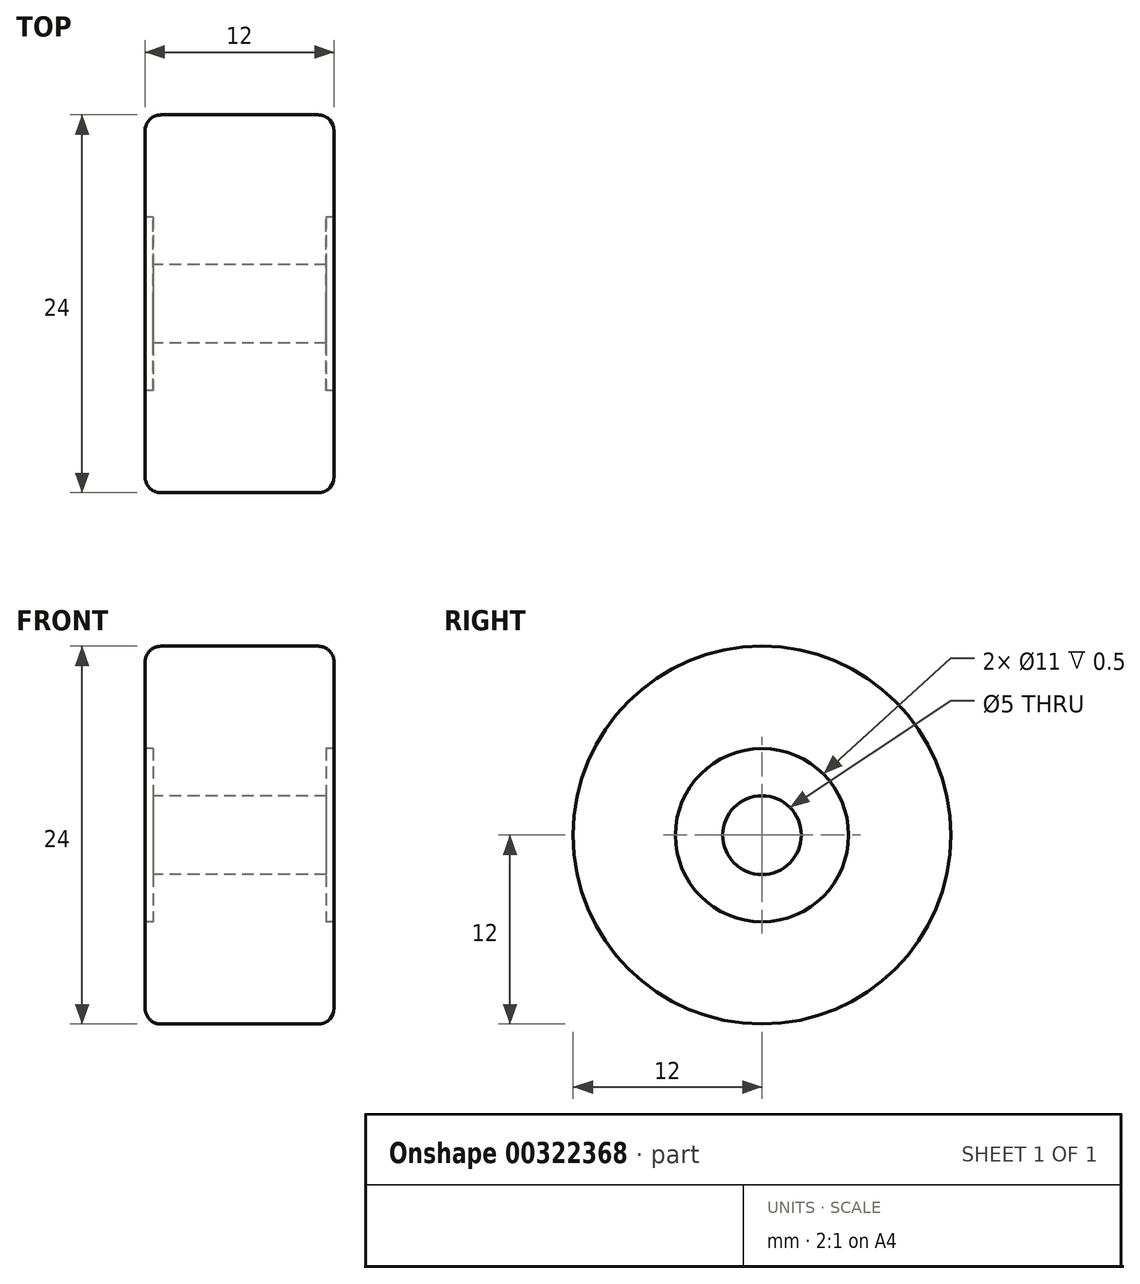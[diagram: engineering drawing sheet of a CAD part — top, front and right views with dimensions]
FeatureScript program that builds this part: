
annotation { "Feature Type Name" : "Feature", "Feature Type Description" : "" }
export const myFeature = defineFeature(function(context is Context, id is Id, definition is map)
    precondition{}
    {
        {
            var Q0;
            Q0=qCreatedBy(makeId("Top.planeOp"),FACE);
            var sketch = newSketch(context, id + "F0", { "sketchPlane" : qUnion([Q0])});
            skLineSegment(sketch, "E0.bottom", {"start": v(0, 0) * mm, "end": v(12, 0) * mm});
            skLineSegment(sketch, "E0.top", {"start": v(1, 12) * mm, "end": v(11, 12) * mm});
            skLineSegment(sketch, "E0.left", {"start": v(0, 0) * mm, "end": v(0, 11) * mm});
            skLineSegment(sketch, "E0.right", {"start": v(12, 0) * mm, "end": v(12, 11) * mm});
            skLineSegment(sketch, "E1", {"start": v(0, 2.5) * mm, "end": v(12, 2.5) * mm});
            skPoint(sketch, "E2.visualSharp", {"position": v(0, 12) * mm});
            skArc(sketch, "E2.filletArc", {"start": v(1, 12) * mm, "mid": v(0.3, 11.7) * mm, "end": v(0, 11) * mm});
            skPoint(sketch, "E3.visualSharp", {"position": v(12, 12) * mm});
            skArc(sketch, "E3.filletArc", {"start": v(12, 11) * mm, "mid": v(11.7, 11.7) * mm, "end": v(11, 12) * mm});
            skLineSegment(sketch, "E4", {"start": v(0, 5.5) * mm, "end": v(0.5, 5.5) * mm});
            skPoint(sketch, "E4.endSnap0", {"position": v(0, 5.5) * mm});
            skLineSegment(sketch, "E5", {"start": v(0.5, 5.5) * mm, "end": v(0.5, 2.5) * mm});
            skLineSegment(sketch, "E6", {"start": v(12, 5.5) * mm, "end": v(11.5, 5.5) * mm});
            skPoint(sketch, "E6.endSnap0", {"position": v(12, 5.5) * mm});
            skLineSegment(sketch, "E7", {"start": v(11.5, 5.5) * mm, "end": v(11.5, 2.5) * mm});
            skSolve(sketch);
        }
        {
            var Q0;
            Q0=makeQuery(id+"F0.imprint","IMPRINT",FACE,{"disambiguationData":[TD([[makeQuery(id+"F0.imprint","IMPRINT",EDGE,{"derivedFrom":sQuery(id+"F0.wireOp",EDGE,"E0.top")}),-1.0]])]});
            var Q1;
            Q1=sQuery(id+"F0.wireOp",EDGE,"E0.bottom");
            revolve(context, id + "F1", {"entities" : qUnion([Q0]), "axis" : qUnion([Q1]), "revolveType" : RevolveType.FULL});
        }
    });
